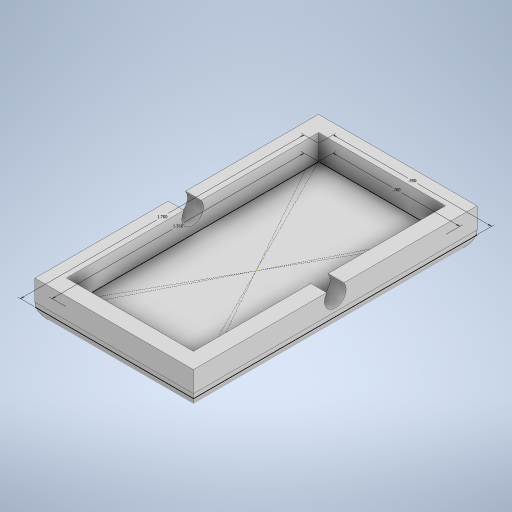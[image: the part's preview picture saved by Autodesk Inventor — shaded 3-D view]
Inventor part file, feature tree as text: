
AUTODESK INVENTOR PART (.ipt)
format: ipt  version: 2024.1 (Build 281209000, 209)  size: 275,456 bytes
history: native  units: in
note: dims shown in document units (in); Inventor stores cm internally (conversion verified against a paired STEP export)
features: sketch x2, extrude x2, hole x1, fillet x1
ambient origin geometry x8: Origin, YZ Plane, XZ Plane, XY Plane, X Axis, Y Axis, Z Axis, Center Point
bodies: Solid1 (feature_tree)
feature tree (6):
  sketch  "Sketch1"  dims[d0=0.95in d1=1.7in]
  extrude  "Extrusion1"  Depth=1.7in
  extrude  "Extrusion2"  Depth=1.51in
  hole  "Hole1"  [1 undecoded]
  fillet  "Fillet1"  Radius=0.1in
  sketch  "Sketch2"  dims[d2=0.76in d3=1.51in d4=0.15in d5=0.0in d6=0.1in d7=0.0in d8=0.11in d9=0.13in d10=0.75in d11=0.375in d12=0.25in d13=0.5635in d14=1.0in d15=0.8108in d16=0.125in]
note: 1 required parameter value undecoded (feature->parameter linkage not recoverable at this tier; creation-order binding heuristic only, values carry confidence <= 0.55)
